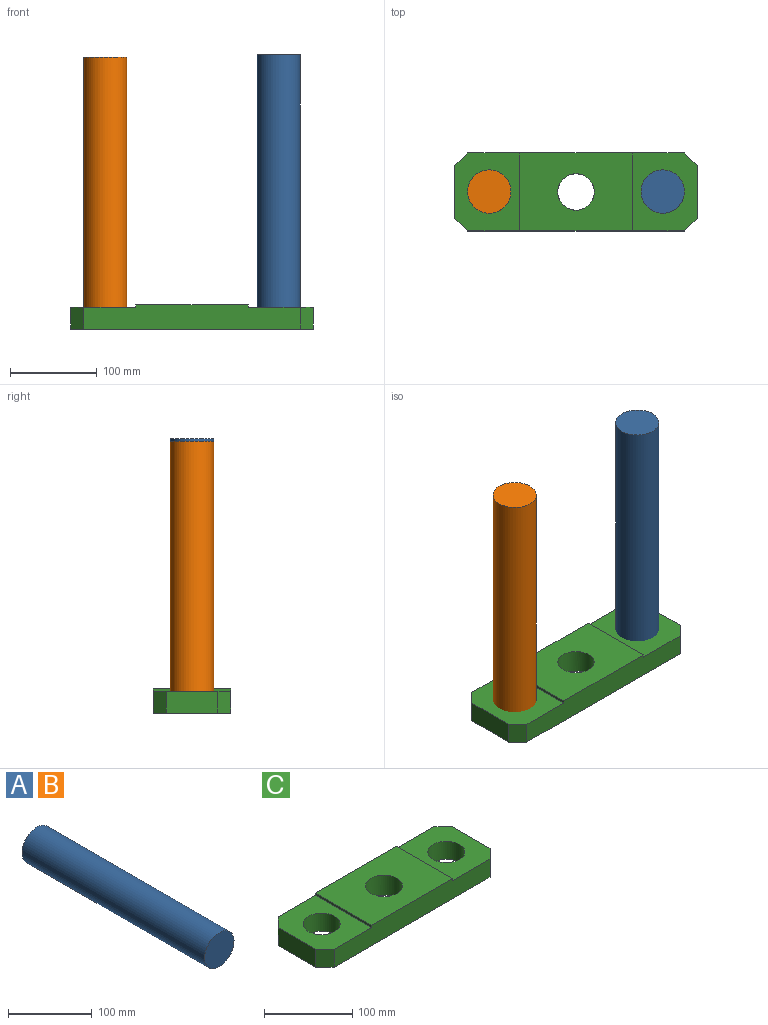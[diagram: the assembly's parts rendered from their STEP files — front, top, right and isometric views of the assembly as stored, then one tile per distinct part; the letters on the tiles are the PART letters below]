
ASSEMBLY  parts=3 mates=3
PART A: 3 faces, bbox 50x309x50 mm
  f0: plane 50x50mm, normal (0,-1,0), area 1963.5mm2, adj f2
  f1: plane 50x50mm, normal (0,1,0), area 1963.5mm2, adj f2
  f2: cylinder r=25mm len=309mm, axis (0,-1,0), area 48537.6mm2, adj f0,f1
PART B: same geometry as A
PART C: 17 faces, bbox 280x90x28 mm
  f0: plane 60x25mm, normal (1,0,0), area 1500mm2, adj f2,f3,f15,f16
  f1: plane 60x25mm, normal (-1,0,0), area 1500mm2, adj f2,f4,f13,f14
  f2: plane 280x90mm, normal (0,0,-1), area 20593.7mm2, adj f0,f1,f5,f6,f10,f11,f12,f13
  f3: plane 90x75mm, normal (0,0,1), area 5139.6mm2, adj f0,f5,f6,f7,f10,f15,f16
  f4: plane 90x75mm, normal (0,0,1), area 5139.6mm2, adj f1,f5,f6,f9,f12,f13,f14
  f5: plane 250x28mm, normal (0,-1,0), area 6640mm2, adj f2,f3,f4,f7,f8,f9,f14,f15
  f6: plane 250x28mm, normal (0,1,0), area 6640mm2, adj f2,f3,f4,f7,f8,f9,f13,f16
  f7: plane 90x3mm, normal (1,0,0), area 270mm2, adj f3,f5,f6,f8
  f8: plane 130x90mm, normal (0,0,1), area 10314.6mm2, adj f5,f6,f7,f9,f11
  f9: plane 90x3mm, normal (-1,0,0), area 270mm2, adj f4,f5,f6,f8
  f10: cylinder r=21mm len=42mm, axis (0,0,1), area 3298.7mm2, adj f2,f3
  f11: cylinder r=21mm len=42mm, axis (0,0,1), area 3694.5mm2, adj f2,f8
  f12: cylinder r=21mm len=42mm, axis (0,0,1), area 3298.7mm2, adj f2,f4
  f13: plane 25x15mm, normal (-0.71,0.71,0), area 530.3mm2, adj f1,f2,f4,f6
  f14: plane 25x15mm, normal (-0.71,-0.71,0), area 530.3mm2, adj f1,f2,f4,f5
  f15: plane 25x15mm, normal (0.71,-0.71,0), area 530.3mm2, adj f0,f2,f3,f5
  f16: plane 25x15mm, normal (0.71,0.71,0), area 530.3mm2, adj f0,f2,f3,f6
PLACE A rot(axis=(-1,0,0),90deg) t=(576.81,115.11,261.15)mm
PLACE B rot(axis=(-1,0,0),90deg) t=(376.81,115.11,258.65)mm
PLACE C rot(axis=(0,0,-1),180deg) t=(476.81,115.11,-5.62)mm
MATE cylindrical B.f2 <-> C.f10  axis (0,0,1) through (376.81,115.11,142.68)mm
MATE parallel A.f2 <-> C.f12  axis (0,0,-1) through (576.81,115.11,-9.32)mm
MATE parallel C.f10 <-> B.f2  axis (0,0,-1) through (376.81,115.11,-16.82)mm
